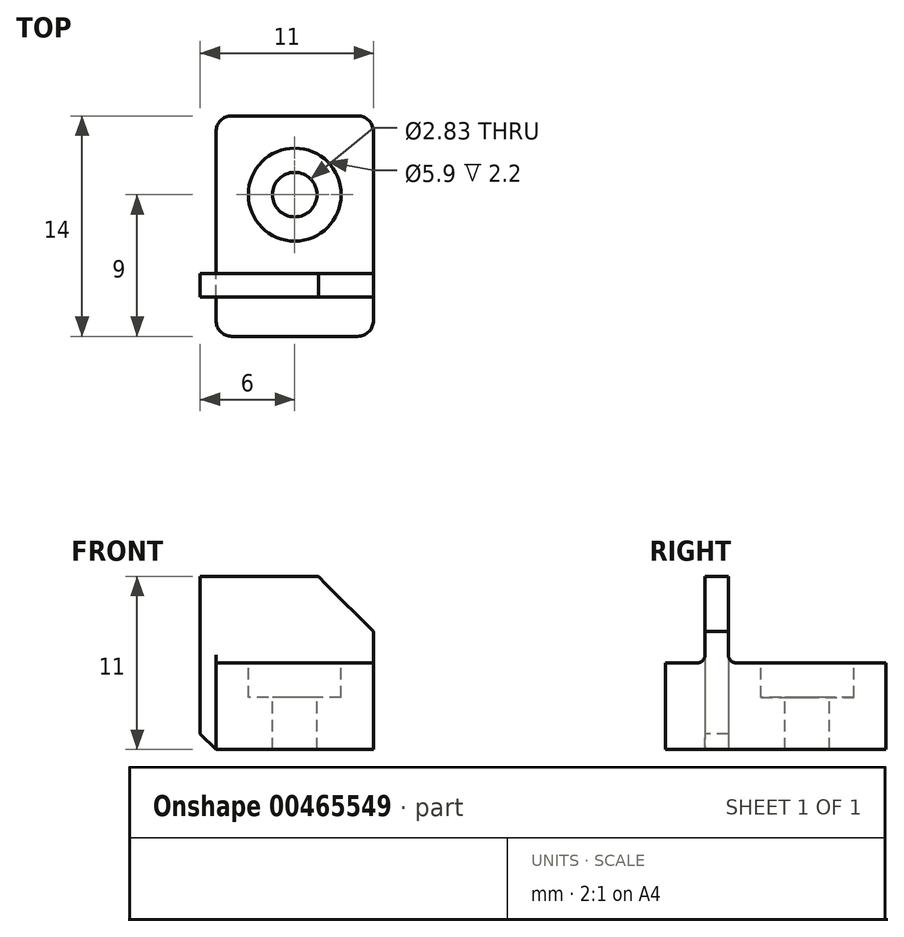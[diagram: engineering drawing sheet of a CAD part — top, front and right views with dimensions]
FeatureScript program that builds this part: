
annotation { "Feature Type Name" : "Feature", "Feature Type Description" : "" }
export const myFeature = defineFeature(function(context is Context, id is Id, definition is map)
    precondition{}
    {
        {
            var Q0;
            Q0=qCreatedBy(makeId("Top.planeOp"),FACE);
            var sketch = newSketch(context, id + "F0", { "sketchPlane" : qUnion([Q0])});
            skLineSegment(sketch, "E0.bottom", {"start": v(0, 0) * mm, "end": v(10, 0) * mm});
            skLineSegment(sketch, "E0.top", {"start": v(0, 14) * mm, "end": v(10, 14) * mm});
            skLineSegment(sketch, "E0.left", {"start": v(0, 0) * mm, "end": v(0, 14) * mm});
            skLineSegment(sketch, "E0.right", {"start": v(10, 0) * mm, "end": v(10, 14) * mm});
            skSolve(sketch);
        }
        {
            var Q0;
            Q0 = qSketchRegion(id + "F0", true);
            extrude(context, id + "F1", {"entities" : qUnion([Q0]), "depth" : 5.5 * mm});
        }
        {
            var Q0;
            Q0=qCreatedBy(makeId("Top.planeOp"),FACE);
            var sketch = newSketch(context, id + "F2", { "sketchPlane" : qUnion([Q0])});
            skLineSegment(sketch, "E1.bottom", {"start": v(-1, 4) * mm, "end": v(7, 4) * mm});
            skLineSegment(sketch, "E1.top", {"start": v(-1, 2.5) * mm, "end": v(7, 2.5) * mm});
            skLineSegment(sketch, "E1.left", {"start": v(-1, 4) * mm, "end": v(-1, 2.5) * mm});
            skLineSegment(sketch, "E1.right", {"start": v(7, 4) * mm, "end": v(7, 2.5) * mm});
            skSolve(sketch);
        }
        {
            var Q0;
            Q0=makeQuery(id+"F1.opExtrude","CAP_FACE",FACE,{"disambiguationData":[OSD([sQuery(id+"F0.wireOp",EDGE,"E0.bottom"),sQuery(id+"F0.wireOp",EDGE,"E0.top"),sQuery(id+"F0.wireOp",EDGE,"E0.left"),sQuery(id+"F0.wireOp",EDGE,"E0.right")])],"isStart":false});
            var sketch = newSketch(context, id + "F3", { "sketchPlane" : qUnion([Q0])});
            skPoint(sketch, "E2", {"position": v(5, 9) * mm});
            skSolve(sketch);
        }
        {
            var Q0;
            Q0=sQuery(id+"F3.wireOp",VERTEX,"E2");
            var Q1;
            Q1=makeQuery(id+"F1.opExtrude","SWEPT_BODY",BODY,{"disambiguationData":[OSD([sQuery(id+"F0.wireOp",EDGE,"E0.bottom"),sQuery(id+"F0.wireOp",EDGE,"E0.top"),sQuery(id+"F0.wireOp",EDGE,"E0.left"),sQuery(id+"F0.wireOp",EDGE,"E0.right")])]});
            hole(context, id + "F4", {"style" : HoleStyle.C_BORE, "endStyle" : HoleEndStyle.THROUGH, "holeDiameter" : 2.83 * mm, "cBoreDiameter" : 5.9 * mm, "cBoreDepth" : 2.2 * mm, "tappedDepth" : 12 * mm, "tapClearance" : 3, "locations" : qUnion([Q0]), "scope" : qUnion([Q1])});
        }
        {
            var Q0;
            Q0 = qSketchRegion(id + "F2", true);
            extrude(context, id + "F5", {"entities" : qUnion([Q0]), "operationType" : NewBodyOperationType.ADD, "depth" : 11 * mm});
        }
        {
            var Q0;
            Q0=makeQuery(id+"F5.opExtrude","CAP_EDGE",EDGE,{"disambiguationData":[OSD([sQuery(id+"F2.wireOp",EDGE,"E1.left")])],"isStart":true});
            chamfer(context, id + "F6", {"entities" : qUnion([Q0]), "width" : 1 * mm, "tangentPropagation" : true});
        }
        {
            var Q0;
            Q0=makeQuery(id+"F1.opExtrude","SWEPT_EDGE",EDGE,{"disambiguationData":[OSD([sQuery(id+"F0.wireOp",EDGE,"E0.top"),sQuery(id+"F0.wireOp",EDGE,"E0.left")])]});
            var Q1;
            Q1=makeQuery(id+"F1.opExtrude","SWEPT_EDGE",EDGE,{"disambiguationData":[OSD([sQuery(id+"F0.wireOp",EDGE,"E0.top"),sQuery(id+"F0.wireOp",EDGE,"E0.right")])]});
            var Q2;
            Q2=makeQuery(id+"F1.opExtrude","SWEPT_EDGE",EDGE,{"disambiguationData":[OSD([sQuery(id+"F0.wireOp",EDGE,"E0.bottom"),sQuery(id+"F0.wireOp",EDGE,"E0.right")])]});
            var Q3;
            Q3=makeQuery(id+"F1.opExtrude","SWEPT_EDGE",EDGE,{"disambiguationData":[OSD([sQuery(id+"F0.wireOp",EDGE,"E0.bottom"),sQuery(id+"F0.wireOp",EDGE,"E0.left")])]});
            fillet(context, id + "F7", {"entities" : qUnion([Q0, Q1, Q2, Q3]), "radius" : 1 * mm, "tangentPropagation" : true, "allowEdgeOverflow" : false});
        }
        {
            var Q0;
            Q0=makeQuery(id+"F5.boolean.opBoolean","INTERSECT",EDGE,{"derivedFrom":[makeQuery(id+"F1.opExtrude","CAP_FACE",FACE,{"disambiguationData":[OSD([sQuery(id+"F0.wireOp",EDGE,"E0.bottom"),sQuery(id+"F0.wireOp",EDGE,"E0.top"),sQuery(id+"F0.wireOp",EDGE,"E0.left"),sQuery(id+"F0.wireOp",EDGE,"E0.right")])],"isStart":false}),makeQuery(id+"F5.opExtrude","SWEPT_FACE",FACE,{"disambiguationData":[OSD([sQuery(id+"F2.wireOp",EDGE,"E1.right")])]})]});
            chamfer(context, id + "F8", {"entities" : qUnion([Q0]), "width" : 5 * mm, "tangentPropagation" : true});
        }
        {
            var Q0;
            Q0=makeQuery(id+"F5.opExtrude","CAP_EDGE",EDGE,{"disambiguationData":[OSD([sQuery(id+"F2.wireOp",EDGE,"E1.right")])],"isStart":false});
            chamfer(context, id + "F9", {"entities" : qUnion([Q0]), "width" : .5 * mm, "tangentPropagation" : true});
        }
        {
            var Q0;
            Q0=makeQuery(id+"F5.boolean.opBoolean","INTERSECT",EDGE,{"derivedFrom":[makeQuery(id+"F1.opExtrude","CAP_FACE",FACE,{"disambiguationData":[OSD([sQuery(id+"F0.wireOp",EDGE,"E0.bottom"),sQuery(id+"F0.wireOp",EDGE,"E0.top"),sQuery(id+"F0.wireOp",EDGE,"E0.left"),sQuery(id+"F0.wireOp",EDGE,"E0.right")])],"isStart":false}),makeQuery(id+"F5.opExtrude","SWEPT_FACE",FACE,{"disambiguationData":[OSD([sQuery(id+"F2.wireOp",EDGE,"E1.bottom")])]})]});
            var Q1;
            Q1=makeQuery(id+"F5.boolean.opBoolean","INTERSECT",EDGE,{"derivedFrom":[makeQuery(id+"F1.opExtrude","CAP_FACE",FACE,{"disambiguationData":[OSD([sQuery(id+"F0.wireOp",EDGE,"E0.bottom"),sQuery(id+"F0.wireOp",EDGE,"E0.top"),sQuery(id+"F0.wireOp",EDGE,"E0.left"),sQuery(id+"F0.wireOp",EDGE,"E0.right")])],"isStart":false}),makeQuery(id+"F5.opExtrude","SWEPT_FACE",FACE,{"disambiguationData":[OSD([sQuery(id+"F2.wireOp",EDGE,"E1.top")])]})]});
            fillet(context, id + "F10", {"entities" : qUnion([Q0, Q1]), "radius" : 0.5 * mm, "tangentPropagation" : true, "allowEdgeOverflow" : false});
        }
    });
